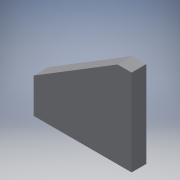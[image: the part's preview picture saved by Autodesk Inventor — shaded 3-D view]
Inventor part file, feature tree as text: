
AUTODESK INVENTOR PART (.ipt)
format: ipt  version: 2019 (Build 230136000, 136)  size: 107,520 bytes
history: native  units: mm
features: other x4, extrude x3, sketch x3, reference x1
ambient origin geometry x8: Origin, YZ Plane, XZ Plane, XY Plane, X Axis, Y Axis, Z Axis, Center Point
bodies: Body1 (feature_tree)
feature tree (11):
  other  "Твердое тело1"
  extrude  "Выдавливание1"  Depth=20.0mm
  extrude  "Выдавливание2"  Depth=6.0mm TaperAngle=0.0deg
  extrude  "Выдавливание3"  Depth=6.0mm TaperAngle=0.0deg
  sketch  "Эскиз1"
  reference  "Ссылка1"
  sketch  "Эскиз2"
  sketch  "Эскиз3"
  parser-record x1  (decoder bookkeeping rows leaked as tree rows — omitted from the tree; the rows remain in map.json)
  other  "kowsh.iam"
  other  "Барабан:1"
note: 1 file-system path scrubbed to <path> (originals preserved in map.json)
